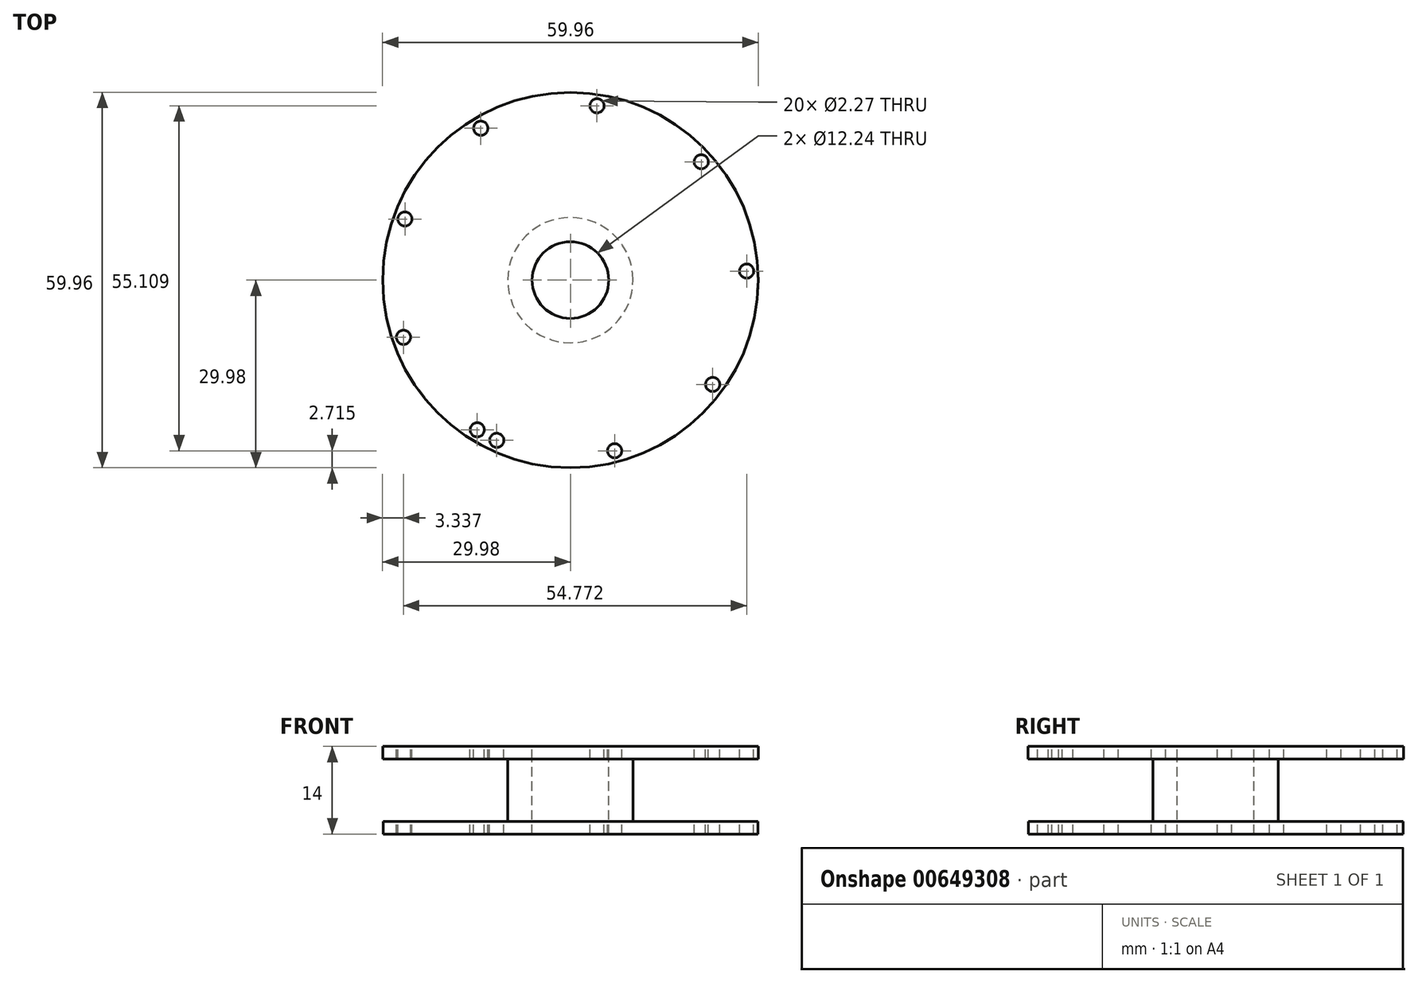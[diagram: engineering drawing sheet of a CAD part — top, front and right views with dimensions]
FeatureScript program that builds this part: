
annotation { "Feature Type Name" : "Feature", "Feature Type Description" : "" }
export const myFeature = defineFeature(function(context is Context, id is Id, definition is map)
    precondition{}
    {
        {
            var Q0;
            Q0=qCreatedBy(makeId("Top.planeOp"),FACE);
            var sketch = newSketch(context, id + "F0", { "sketchPlane" : qUnion([Q0])});
            skCircle(sketch, "E0", {"center": v(0, 0) * mm, "radius": 29.9 * mm});
            skSolve(sketch);
        }
        {
            var Q0;
            Q0 = qSketchRegion(id + "F0", true);
            extrude(context, id + "F1", {"entities" : qUnion([Q0]), "depth" : 2 * mm, "offsetDistance" : 25 * mm});
        }
        {
            var Q0;
            Q0=makeQuery(id+"F1.opExtrude","CAP_FACE",FACE,{"disambiguationData":[OSD([sQuery(id+"F0.wireOp",EDGE,"E0")])],"isStart":false});
            var sketch = newSketch(context, id + "F2", { "sketchPlane" : qUnion([Q0])});
            skCircle(sketch, "E1", {"center": v(0, 0) * mm, "radius": 10 * mm});
            skSolve(sketch);
        }
        {
            var Q0;
            Q0=makeQuery(id+"F2.imprint","IMPRINT",FACE,{"disambiguationData":[TD([[makeQuery(id+"F2.imprint","IMPRINT",EDGE,{"derivedFrom":sQuery(id+"F2.wireOp",EDGE,"E1")}),1.0]])]});
            extrude(context, id + "F3", {"entities" : qUnion([Q0]), "operationType" : NewBodyOperationType.ADD, "depth" : 10 * mm, "offsetDistance" : 25 * mm});
        }
        {
            var Q0;
            Q0=makeQuery(id+"F3.opExtrude","CAP_FACE",FACE,{"disambiguationData":[OSD([sQuery(id+"F2.wireOp",EDGE,"E1")])],"isStart":false});
            var sketch = newSketch(context, id + "F4", { "sketchPlane" : qUnion([Q0])});
            skCircle(sketch, "E2", {"center": v(0, 0) * mm, "radius": 29.98 * mm});
            skSolve(sketch);
        }
        {
            var Q0;
            Q0 = qSketchRegion(id + "F4", true);
            extrude(context, id + "F5", {"entities" : qUnion([Q0]), "depth" : 2 * mm, "offsetDistance" : 25 * mm});
        }
        {
            var Q0;
            Q0=makeQuery(id+"F5.opExtrude","CAP_FACE",FACE,{"disambiguationData":[OSD([sQuery(id+"F4.wireOp",EDGE,"E2")])],"isStart":false});
            var sketch = newSketch(context, id + "F6", { "sketchPlane" : qUnion([Q0])});
            skCircle(sketch, "E3", {"center": v(-14.87, -23.92) * mm, "radius": 1.14 * mm});
            skCircle(sketch, "E4.1.0", {"center": v(-26.64, -9.14) * mm, "radius": 1.14 * mm});
            skCircle(sketch, "E4.2.0", {"center": v(-26.42, 9.76) * mm, "radius": 1.14 * mm});
            skCircle(sketch, "E4.3.0", {"center": v(-14.3, 24.26) * mm, "radius": 1.14 * mm});
            skCircle(sketch, "E4.4.0", {"center": v(4.25, 27.84) * mm, "radius": 1.14 * mm});
            skCircle(sketch, "E4.5.0", {"center": v(20.89, 18.9) * mm, "radius": 1.14 * mm});
            skCircle(sketch, "E4.6.0", {"center": v(28.13, 1.44) * mm, "radius": 1.14 * mm});
            skCircle(sketch, "E4.7.0", {"center": v(22.7, -16.66) * mm, "radius": 1.14 * mm});
            skCircle(sketch, "E4.8.0", {"center": v(7.07, -27.27) * mm, "radius": 1.14 * mm});
            skCircle(sketch, "E4.9.0", {"center": v(-11.76, -25.6) * mm, "radius": 1.14 * mm});
            skPoint(sketch, "E4.center", {"position": v(0, 0) * mm});
            skLineSegment(sketch, "E4.anchor1", {"start": v(0, 0) * mm, "end": v(-14.87, -23.92) * mm, "construction": true});
            skLineSegment(sketch, "E4.anchor2", {"start": v(0, 0) * mm, "end": v(-11.76, -25.6) * mm, "construction": true});
            skSolve(sketch);
        }
        {
            var Q0;
            Q0 = qSketchRegion(id + "F6", true);
            extrude(context, id + "F7", {"entities" : qUnion([Q0]), "operationType" : NewBodyOperationType.REMOVE, "oppositeDirection" : true, "depth" : 25 * mm, "offsetDistance" : 25 * mm});
        }
        {
            var Q0;
            Q0=makeQuery(id+"F5.opExtrude","CAP_FACE",FACE,{"disambiguationData":[OSD([sQuery(id+"F4.wireOp",EDGE,"E2")])],"isStart":false});
            var sketch = newSketch(context, id + "F8", { "sketchPlane" : qUnion([Q0])});
            skCircle(sketch, "E5", {"center": v(0, 0) * mm, "radius": 6.12 * mm});
            skSolve(sketch);
        }
        {
            var Q0;
            Q0 = qSketchRegion(id + "F8", true);
            extrude(context, id + "F9", {"entities" : qUnion([Q0]), "operationType" : NewBodyOperationType.REMOVE, "oppositeDirection" : true, "depth" : 25 * mm, "offsetDistance" : 25 * mm});
        }
    });
